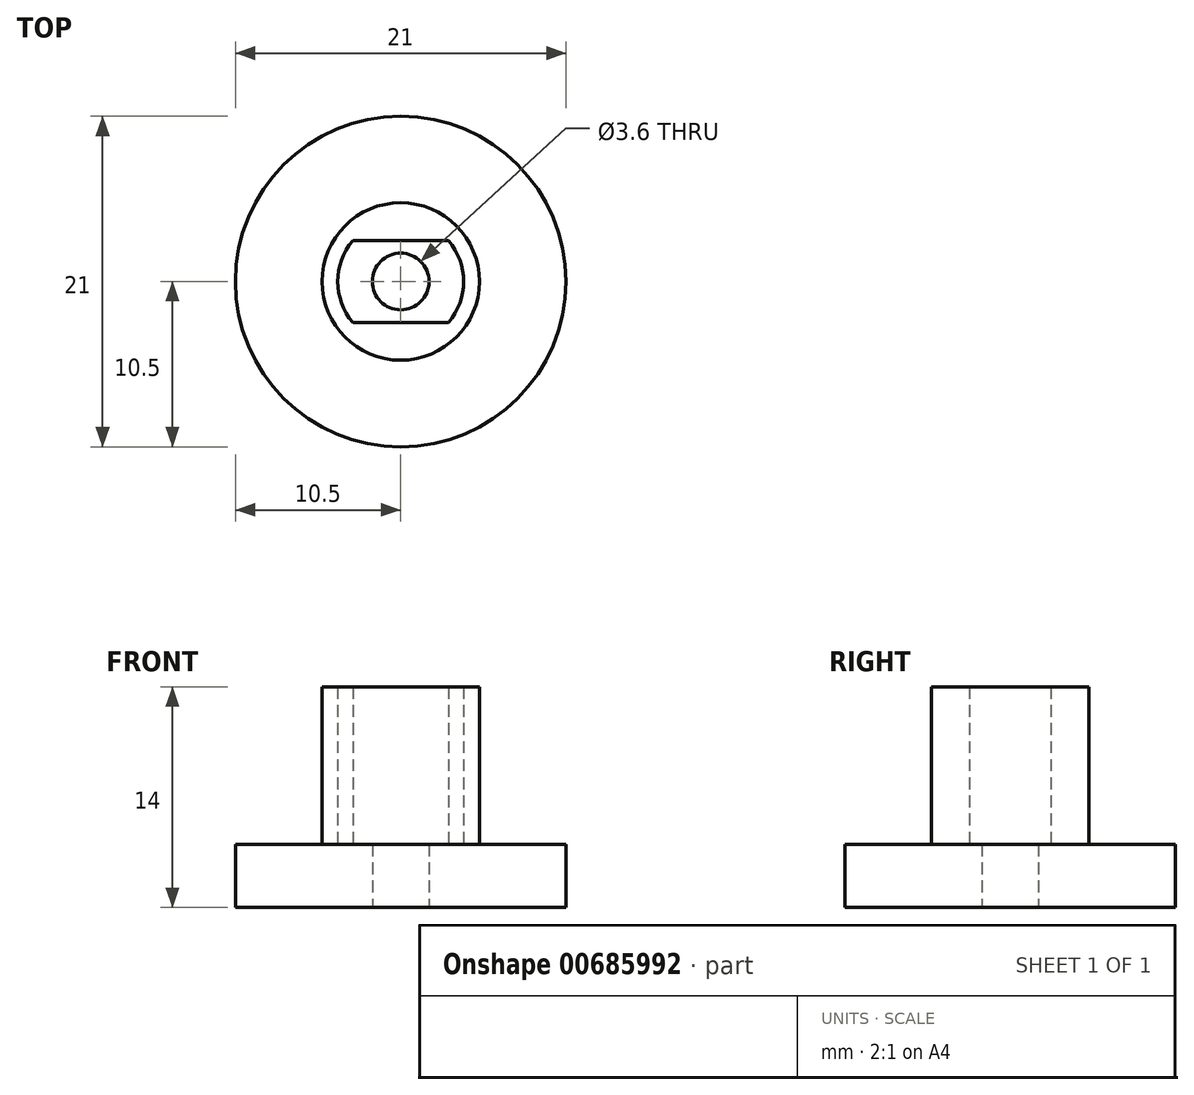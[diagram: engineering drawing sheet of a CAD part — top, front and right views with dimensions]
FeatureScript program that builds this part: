
annotation { "Feature Type Name" : "Feature", "Feature Type Description" : "" }
export const myFeature = defineFeature(function(context is Context, id is Id, definition is map)
    precondition{}
    {
        {
            var Q0;
            Q0=qCreatedBy(makeId("Top.planeOp"),FACE);
            var sketch = newSketch(context, id + "F0", { "sketchPlane" : qUnion([Q0])});
            skCircle(sketch, "E0", {"center": v(0, 0) * mm, "radius": 10.5 * mm});
            skCircle(sketch, "E1", {"center": v(0, 0) * mm, "radius": 5 * mm});
            skArc(sketch, "E2", {"start": v(3.04, -2.6) * mm, "mid": v(4, 0) * mm, "end": v(3.04, 2.6) * mm});
            skLineSegment(sketch, "E3", {"start": v(-3.04, 2.6) * mm, "end": v(3.04, 2.6) * mm});
            skLineSegment(sketch, "E4.MirrorCS", {"start": v(-3.04, -2.6) * mm, "end": v(3.04, -2.6) * mm});
            skPoint(sketch, "E5.orphan", {"position": v(-6.58, 2.6) * mm});
            skPoint(sketch, "E6.orphan", {"position": v(-6.58, -2.6) * mm});
            skPoint(sketch, "E7.trimOffspring.end.orphan", {"position": v(7.22, -2.6) * mm});
            skPoint(sketch, "E8.orphan", {"position": v(7.22, 2.6) * mm});
            skArc(sketch, "E9.trimOffspring", {"start": v(-3.04, 2.6) * mm, "mid": v(-4, 0) * mm, "end": v(-3.04, -2.6) * mm});
            skCircle(sketch, "E10", {"center": v(0, 0) * mm, "radius": 1.8 * mm});
            skSolve(sketch);
        }
        {
            var Q0;
            Q0=makeQuery(id+"F0.imprint","IMPRINT",FACE,{"disambiguationData":[TD([[makeQuery(id+"F0.imprint","IMPRINT",EDGE,{"derivedFrom":sQuery(id+"F0.wireOp",EDGE,"E0")}),1.0]])]});
            var Q1;
            Q1=makeQuery(id+"F0.imprint","IMPRINT",FACE,{"disambiguationData":[TD([[makeQuery(id+"F0.imprint","IMPRINT",EDGE,{"derivedFrom":sQuery(id+"F0.wireOp",EDGE,"E1")}),1.0]])]});
            var Q2;
            Q2=makeQuery(id+"F0.imprint","IMPRINT",FACE,{"disambiguationData":[TD([[makeQuery(id+"F0.imprint","IMPRINT",EDGE,{"derivedFrom":sQuery(id+"F0.wireOp",EDGE,"E2")}),1.0]])]});
            extrude(context, id + "F1", {"entities" : qUnion([Q0, Q1, Q2]), "depth" : 4 * mm, "offsetDistance" : 25 * mm});
        }
        {
            var Q0;
            Q0=makeQuery(id+"F0.imprint","IMPRINT",FACE,{"disambiguationData":[TD([[makeQuery(id+"F0.imprint","IMPRINT",EDGE,{"derivedFrom":sQuery(id+"F0.wireOp",EDGE,"E1")}),1.0]])]});
            extrude(context, id + "F2", {"entities" : qUnion([Q0]), "operationType" : NewBodyOperationType.ADD, "depth" : 14 * mm, "offsetDistance" : 25 * mm});
        }
    });
